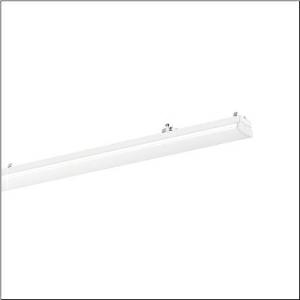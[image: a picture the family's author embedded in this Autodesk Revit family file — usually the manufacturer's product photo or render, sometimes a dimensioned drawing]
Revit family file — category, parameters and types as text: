
# Revit family: licross_11_recessed_opal_ho_51tl1ddn4d5m
name_source: partatom
category: Lighting Fixtures
units: mm (PartAtom-declared; Revit-internal decimal feet)

## family parameters
Cut with Voids When Loaded = No
Host = Face
Light Source = No
Part Type = Normal
Room Calculation Point = No
Round Connector Dimension = Use Diameter
Shared = No

## types (1)
- --- (1 x LED, 13620 lm, 76.8 W, 4000K)
    Apparent Load = 77 VA
    CIE Flux Codes = 44 73 91 87 100
    Color Rendering = 80
    Color Temperature = 4000K
    Default Elevation = 1800 mm
    Description = Licross 11 recessed opal HO, luminaire insert, of sheet steel, coil coated, white, length: 1.500mm, width: 76mm, height: 87mm, LED rated luminous flux: 13.620lm, light colour: 840, SDCM (Standard Deviation of Colour Matching)MacAdam ≤ 2 SDCM (initial), control gear: DALI 2, with plug, 5-pole, with phase selection, mains connection: 220..240V, AC, 50/60Hz, rated input power: 77W, internal wiring halogen-free, primary optical cover: cover, of PMMA, light emission: direct with ceiling illumination distribution, primary light characteristic: symmetric, protection rating (complete): IP40, insulation class (complete): insulation class I (protective earthing), certification: CE, ENEC, VDE, UKCA, protection symbol: D if used in an environment without relevant dust loads with corresponding accessories, impact resistance: IK06, permissible ambient temperature for indoor applications: -25..+30°C, corresponds to IFS (International Featured Standards) requirements for safety and quality in the food industry, reducing of maximum allowable ambient temperature of 5°C with ceiling mounting, LABS conformity tested according to VDMA 24364:2018-05, The light source and the operating device comply with the requirements of the Ecodesign Regulation (EU) 2019/2020 and are replaceable in accordance with this regulation, packaging unit: 1 piece
    Height = 83 mm
    Lamp = 1 x LED
    Lamp Light Flux = 13620 lm
    Lamp Power = 76.8 W
    Lamp count = 1
    Length = 1500 mm
    Luminous efficacy = 177 lm/W
    Manufacturer = Siteco
    ModVariant = No
    Model = 51TL1DDN4D5M
    Mounting Place = Ceiling
    Mounting Type = Pendant
    Number of Poles = 1
    OnlyDefault = Yes
    Power Factor = 1
    Product Name = Licross 11 recessed opal HO
    Product group = luminaire insert | ceiling pendant
    ProductGroupID = 901
    Protection Class = Protection class I
    Protection Degree = IP 40
    RLX_Detail_Level = 1
    RLX_Emergency_Light_Flux = 0 lm
    RLX_Emergency_Type = 0
    RLX_Emergency_Type_DB = No
    RlxData = <blob elided: 27225 chars, md5=d530f54c>
    Socket = socket
    Standby Power = 0 W
    System Light Flux = 13620 lm
    System Power = 77 W
    Type Comments = factory setting: luminous flux: 100 % | dim-lin: 254 | 522 mA
    Type Image = l_1313666.jpg
    URL = http://relux.com
    VarID = @adj_083807
    Voltage = 0 V
    Weight = 0.00 kg
    Width = 76 mm

## geometry (parser evidence)
native form markers: Blend x4, Sweep x15
no freeform markers — native parametric forms only
